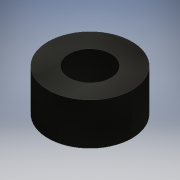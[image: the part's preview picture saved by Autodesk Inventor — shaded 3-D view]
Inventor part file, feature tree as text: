
AUTODESK INVENTOR PART (.ipt)
format: ipt  version: 2020.2 (Build 242310000, 310)  size: 95,232 bytes
history: native  units: mm
features: other x1, extrude x1, sketch x1
ambient origin geometry x8: Origin, YZ Plane, XZ Plane, XY Plane, X Axis, Y Axis, Z Axis, Center Point
bodies: Body1 (feature_tree)
feature tree (3):
  other  "ソリッド1"
  extrude  "押し出し1"  Depth=6.0mm
  sketch  "スケッチ1"
